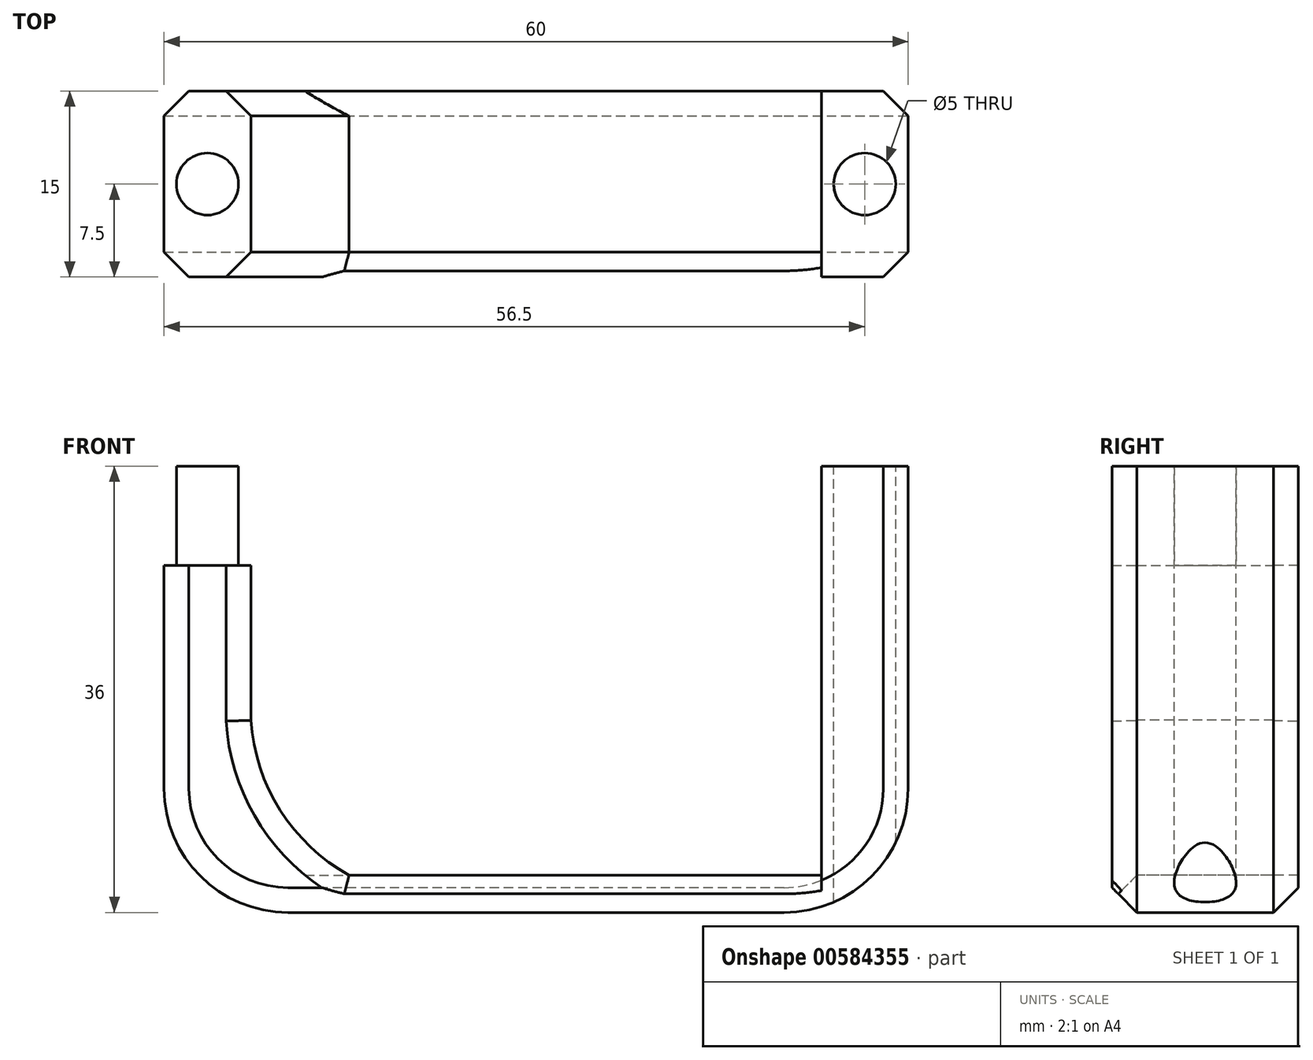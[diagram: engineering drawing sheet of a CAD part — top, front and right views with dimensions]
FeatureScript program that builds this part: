
annotation { "Feature Type Name" : "Feature", "Feature Type Description" : "" }
export const myFeature = defineFeature(function(context is Context, id is Id, definition is map)
    precondition{}
    {
        {
            var Q0;
            Q0=qCreatedBy(makeId("Top.planeOp"),FACE);
            var sketch = newSketch(context, id + "F0", { "sketchPlane" : qUnion([Q0])});
            skLineSegment(sketch, "E0.bottom", {"start": v(-30, 7.5) * mm, "end": v(30, 7.5) * mm});
            skLineSegment(sketch, "E0.top", {"start": v(-30, -7.5) * mm, "end": v(30, -7.5) * mm});
            skLineSegment(sketch, "E0.left", {"start": v(-30, 7.5) * mm, "end": v(-30, -7.5) * mm});
            skLineSegment(sketch, "E0.right", {"start": v(30, 7.5) * mm, "end": v(30, -7.5) * mm});
            skPoint(sketch, "E0.middle", {"position": v(0, 0) * mm});
            skLineSegment(sketch, "E1", {"start": v(-23, -7.5) * mm, "end": v(-23, 7.5) * mm});
            skLineSegment(sketch, "E2", {"start": v(23, 7.5) * mm, "end": v(23, -7.5) * mm});
            skCircle(sketch, "E3", {"center": v(-26.5, 0) * mm, "radius": 2.5 * mm});
            skCircle(sketch, "E4.MirrorC", {"center": v(26.5, 0) * mm, "radius": 2.5 * mm});
            skSolve(sketch);
        }
        {
            var Q0;
            {var subQ0=sQuery(id+"F0.wireOp",EDGE,"E0.left");Q0=makeQuery(id+"F0.imprint","IMPRINT",FACE,{"disambiguationData":[TD([[makeQuery(id+"F0.imprint","IMPRINT",EDGE,{"derivedFrom":subQ0}),1.0]])]});}
            var Q1;
            {var subQ1=sQuery(id+"F0.wireOp",EDGE,"E0.right");Q1=makeQuery(id+"F0.imprint","IMPRINT",FACE,{"disambiguationData":[TD([[makeQuery(id+"F0.imprint","IMPRINT",EDGE,{"derivedFrom":subQ1}),-1.0]])]});}
            extrude(context, id + "F1", {"entities" : qUnion([Q0, Q1]), "depth" : 25 * mm, "offsetDistance" : 25 * mm});
        }
        {
            var Q0;
            Q0=makeQuery(id+"F0.imprint","IMPRINT",FACE,{"disambiguationData":[TD([[makeQuery(id+"F0.imprint","IMPRINT",EDGE,{"derivedFrom":sQuery(id+"F0.wireOp",EDGE,"E3")}),1.0]])]});
            var Q1;
            Q1=makeQuery(id+"F0.imprint","IMPRINT",FACE,{"disambiguationData":[TD([[makeQuery(id+"F0.imprint","IMPRINT",EDGE,{"derivedFrom":sQuery(id+"F0.wireOp",EDGE,"E4.MirrorC")}),-1.0]])]});
            extrude(context, id + "F2", {"entities" : qUnion([Q0, Q1]), "depth" : 33 * mm, "offsetDistance" : 25 * mm});
        }
        {
            var Q0;
            {var subQ0=sQuery(id+"F0.wireOp",EDGE,"E1");Q0=makeQuery(id+"F0.imprint","IMPRINT",FACE,{"disambiguationData":[TD([[makeQuery(id+"F0.imprint","IMPRINT",EDGE,{"derivedFrom":subQ0}),-1.0]])]});}
            var Q1;
            {var subQ0=sQuery(id+"F0.wireOp",EDGE,"E0.left");Q1=makeQuery(id+"F0.imprint","IMPRINT",FACE,{"disambiguationData":[TD([[makeQuery(id+"F0.imprint","IMPRINT",EDGE,{"derivedFrom":subQ0}),1.0]])]});}
            var Q2;
            {var subQ1=sQuery(id+"F0.wireOp",EDGE,"E0.right");Q2=makeQuery(id+"F0.imprint","IMPRINT",FACE,{"disambiguationData":[TD([[makeQuery(id+"F0.imprint","IMPRINT",EDGE,{"derivedFrom":subQ1}),-1.0]])]});}
            var Q3;
            Q3=makeQuery(id+"F0.imprint","IMPRINT",FACE,{"disambiguationData":[TD([[makeQuery(id+"F0.imprint","IMPRINT",EDGE,{"derivedFrom":sQuery(id+"F0.wireOp",EDGE,"E4.MirrorC")}),-1.0]])]});
            var Q4;
            Q4=makeQuery(id+"F0.imprint","IMPRINT",FACE,{"disambiguationData":[TD([[makeQuery(id+"F0.imprint","IMPRINT",EDGE,{"derivedFrom":sQuery(id+"F0.wireOp",EDGE,"E3")}),1.0]])]});
            extrude(context, id + "F3", {"entities" : qUnion([Q0, Q1, Q2, Q3, Q4]), "oppositeDirection" : true, "depth" : 3 * mm, "offsetDistance" : 25 * mm});
        }
        {
            var Q0;
            Q0=makeQuery(id+"F2.opExtrude","SWEPT_BODY",BODY,{"disambiguationData":[OSD([sQuery(id+"F0.wireOp",EDGE,"E3")])]});
            var Q1;
            Q1=makeQuery(id+"F3.opExtrude","SWEPT_BODY",BODY,{"disambiguationData":[OSD([sQuery(id+"F0.wireOp",EDGE,"E0.bottom"),sQuery(id+"F0.wireOp",EDGE,"E0.top"),sQuery(id+"F0.wireOp",EDGE,"E0.left"),sQuery(id+"F0.wireOp",EDGE,"E0.right")])]});
            var Q2;
            Q2=makeQuery(id+"F1.opExtrude","SWEPT_BODY",BODY,{"disambiguationData":[OSD([sQuery(id+"F0.wireOp",EDGE,"E0.bottom"),sQuery(id+"F0.wireOp",EDGE,"E0.top"),sQuery(id+"F0.wireOp",EDGE,"E0.left"),sQuery(id+"F0.wireOp",EDGE,"E1"),sQuery(id+"F0.wireOp",EDGE,"E3")])]});
            var Q3;
            Q3=makeQuery(id+"F2.opExtrude","SWEPT_BODY",BODY,{"disambiguationData":[OSD([sQuery(id+"F0.wireOp",EDGE,"E4.MirrorC")])]});
            var Q4;
            Q4=makeQuery(id+"F1.opExtrude","SWEPT_BODY",BODY,{"disambiguationData":[OSD([sQuery(id+"F0.wireOp",EDGE,"E0.bottom"),sQuery(id+"F0.wireOp",EDGE,"E0.top"),sQuery(id+"F0.wireOp",EDGE,"E0.right"),sQuery(id+"F0.wireOp",EDGE,"E2"),sQuery(id+"F0.wireOp",EDGE,"E4.MirrorC")])]});
            booleanBodies(context, id + "F4", {"operationType" : BooleanOperationType.UNION, "tools" : qUnion([Q0, Q1, Q2, Q3, Q4])});
        }
        {
            var Q0;
            {var subQ0=sQuery(id+"F0.wireOp",EDGE,"E0.top");Q0=makeQuery(id+"F4.opBoolean","MERGE",FACE,{"derivedFrom":[makeQuery(id+"F1.opExtrude","SWEPT_FACE",FACE,{"disambiguationData":[OSD([subQ0]),TDD([makeQuery(id+"F0.imprint","IMPRINT",EDGE,{"disambiguationData":[TD([[makeQuery(id+"F0.imprint","INTERSECT",VERTEX,{"derivedFrom":[subQ0,sQuery(id+"F0.wireOp",EDGE,"E0.left")]}),-1.0]])],"derivedFrom":subQ0})])]}),makeQuery(id+"F1.opExtrude","SWEPT_FACE",FACE,{"disambiguationData":[OSD([subQ0]),TDD([makeQuery(id+"F0.imprint","IMPRINT",EDGE,{"disambiguationData":[TD([[makeQuery(id+"F0.imprint","INTERSECT",VERTEX,{"derivedFrom":[subQ0,sQuery(id+"F0.wireOp",EDGE,"E0.right")]}),1.0]])],"derivedFrom":subQ0})])]}),makeQuery(id+"F3.opExtrude","SWEPT_FACE",FACE,{"disambiguationData":[OSD([subQ0])]})]});}
            var sketch = newSketch(context, id + "F5", { "sketchPlane" : qUnion([Q0])});
            skArc(sketch, "E5", {"start": v(-23, 12.5) * mm, "mid": v(-14.94, -0.08) * mm, "end": v(0, 0) * mm});
            skArc(sketch, "E6.MirrorCS", {"start": v(23, 12.5) * mm, "mid": v(14.94, -0.08) * mm, "end": v(0, 0) * mm});
            skSolve(sketch);
        }
        {
            var Q0;
            {var subQ0=sQuery(id+"F5.wireOp",EDGE,"E5");var subQ1=sQuery(id+"F0.wireOp",EDGE,"E0.top");var subQ4=makeQuery(id+"F3.opExtrude","CAP_EDGE",EDGE,{"disambiguationData":[OSD([subQ1])],"isStart":true});var subQ5=makeQuery(id+"F5.imprint","INTERSECT",VERTEX,{"derivedFrom":[subQ4,subQ0]});Q0=makeQuery(id+"F5.imprint","IMPRINT",FACE,{"disambiguationData":[TD([[makeQuery(id+"F5.imprint","IMPRINT",EDGE,{"disambiguationData":[TD([[subQ5,1.0]])],"derivedFrom":subQ0}),-1.0]])]});}
            var Q1;
            {var subQ0=sQuery(id+"F5.wireOp",EDGE,"E6.MirrorCS");var subQ1=sQuery(id+"F0.wireOp",EDGE,"E0.top");var subQ4=makeQuery(id+"F3.opExtrude","CAP_EDGE",EDGE,{"disambiguationData":[OSD([subQ1])],"isStart":true});var subQ5=makeQuery(id+"F5.imprint","INTERSECT",VERTEX,{"derivedFrom":[subQ4,subQ0]});Q1=makeQuery(id+"F5.imprint","IMPRINT",FACE,{"disambiguationData":[TD([[makeQuery(id+"F5.imprint","IMPRINT",EDGE,{"disambiguationData":[TD([[subQ5,1.0]])],"derivedFrom":subQ0}),1.0]])]});}
            extrude(context, id + "F6", {"entities" : qUnion([Q0, Q1]), "operationType" : NewBodyOperationType.ADD, "oppositeDirection" : true, "depth" : 15 * mm, "offsetDistance" : 25 * mm});
        }
        {
            var Q0;
            Q0=makeQuery(id+"F3.opExtrude","CAP_EDGE",EDGE,{"disambiguationData":[OSD([sQuery(id+"F0.wireOp",EDGE,"E0.left")])],"isStart":false});
            var Q1;
            Q1=makeQuery(id+"F3.opExtrude","CAP_EDGE",EDGE,{"disambiguationData":[OSD([sQuery(id+"F0.wireOp",EDGE,"E0.right")])],"isStart":false});
            var Q2;
            Q2=makeQuery(id+"F6.opExtrude","SWEPT_EDGE",EDGE,{"disambiguationData":[OSD([sQuery(id+"F0.wireOp",EDGE,"E0.top"),sQuery(id+"F5.wireOp",EDGE,"E6.MirrorCS")])]});
            var Q3;
            Q3=makeQuery(id+"F6.opExtrude","SWEPT_EDGE",EDGE,{"disambiguationData":[OSD([sQuery(id+"F0.wireOp",EDGE,"E0.top"),sQuery(id+"F5.wireOp",EDGE,"E5")])]});
            fillet(context, id + "F7", {"entities" : qUnion([Q0, Q1, Q2, Q3]), "radius" : 10 * mm, "tangentPropagation" : true, "allowEdgeOverflow" : false});
        }
        {
            var Q0;
            Q0=makeQuery(id+"F3.opExtrude","CAP_EDGE",EDGE,{"disambiguationData":[OSD([sQuery(id+"F0.wireOp",EDGE,"E0.top")])],"isStart":false});
            var Q1;
            Q1=makeQuery(id+"F3.opExtrude","CAP_EDGE",EDGE,{"disambiguationData":[OSD([sQuery(id+"F0.wireOp",EDGE,"E0.bottom")])],"isStart":false});
            var Q2;
            Q2=makeQuery(id+"F3.opExtrude","CAP_EDGE",EDGE,{"disambiguationData":[OSD([sQuery(id+"F0.wireOp",EDGE,"E0.top")])],"isStart":true});
            var Q3;
            Q3=makeQuery(id+"F1.opExtrude","SWEPT_EDGE",EDGE,{"disambiguationData":[OSD([sQuery(id+"F0.wireOp",EDGE,"E0.top"),sQuery(id+"F0.wireOp",EDGE,"E2")])]});
            var Q4;
            Q4=makeQuery(id+"F1.opExtrude","SWEPT_EDGE",EDGE,{"disambiguationData":[OSD([sQuery(id+"F0.wireOp",EDGE,"E0.top"),sQuery(id+"F0.wireOp",EDGE,"E1")])]});
            var Q5;
            Q5=makeQuery(id+"F1.opExtrude","SWEPT_EDGE",EDGE,{"disambiguationData":[OSD([sQuery(id+"F0.wireOp",EDGE,"E0.bottom"),sQuery(id+"F0.wireOp",EDGE,"E1")])]});
            var Q6;
            Q6=makeQuery(id+"F1.opExtrude","SWEPT_EDGE",EDGE,{"disambiguationData":[OSD([sQuery(id+"F0.wireOp",EDGE,"E0.bottom"),sQuery(id+"F0.wireOp",EDGE,"E2")])]});
            chamfer(context, id + "F8", {"entities" : qUnion([Q0, Q1, Q2, Q3, Q4, Q5, Q6]), "width" : 2 * mm, "tangentPropagation" : true});
        }
    });
